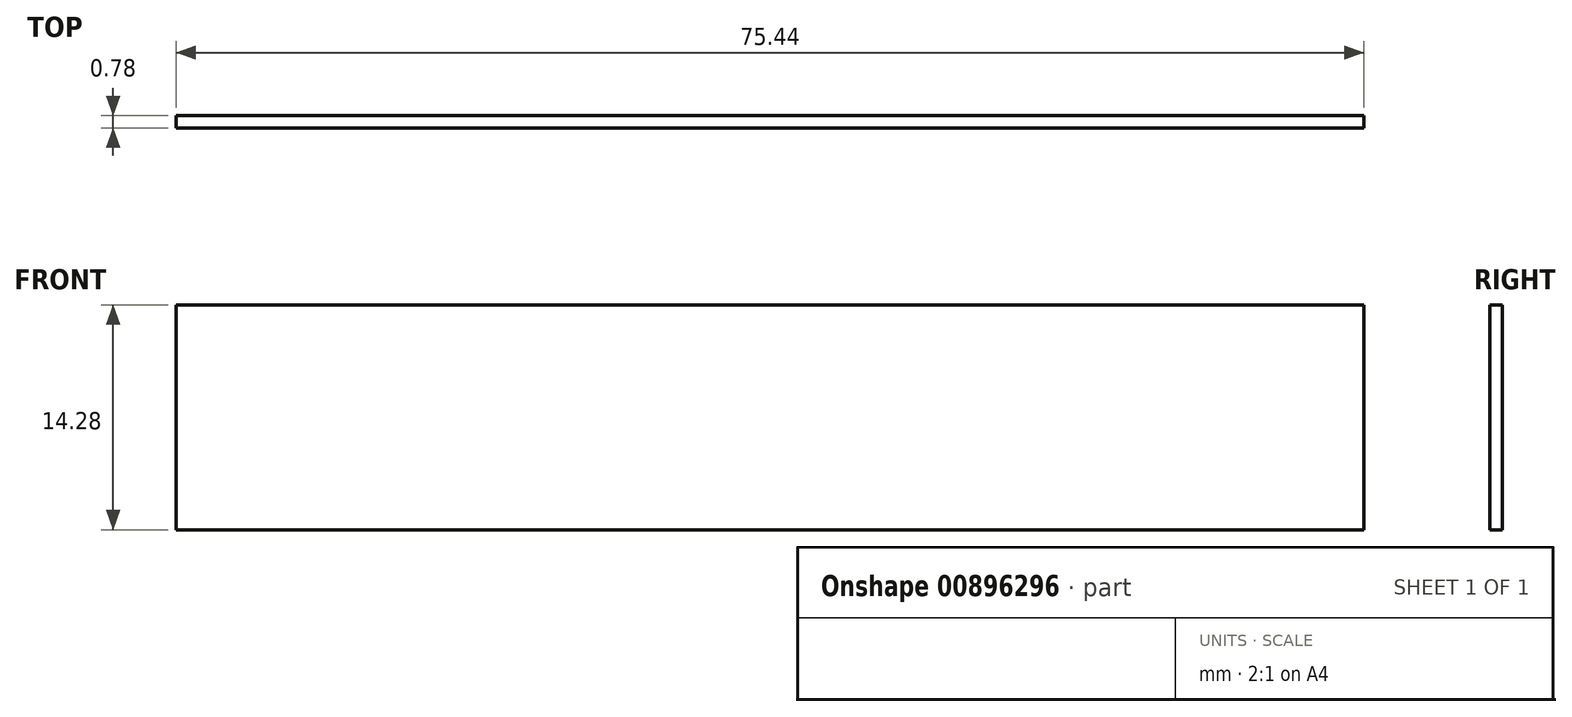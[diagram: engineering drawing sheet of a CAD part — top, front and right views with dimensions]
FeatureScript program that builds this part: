
annotation { "Feature Type Name" : "Feature", "Feature Type Description" : "" }
export const myFeature = defineFeature(function(context is Context, id is Id, definition is map)
    precondition{}
    {
        {
            var Q0;
            Q0=qCreatedBy(makeId("Front.planeOp"),FACE);
            var sketch = newSketch(context, id + "F0", { "sketchPlane" : qUnion([Q0])});
            skLineSegment(sketch, "E0.bottom", {"start": v(37.72, -7.14) * mm, "end": v(-37.72, -7.14) * mm});
            skLineSegment(sketch, "E0.top", {"start": v(37.72, 7.14) * mm, "end": v(-37.72, 7.14) * mm});
            skLineSegment(sketch, "E0.left", {"start": v(37.72, -7.14) * mm, "end": v(37.72, 7.14) * mm});
            skLineSegment(sketch, "E0.right", {"start": v(-37.72, -7.14) * mm, "end": v(-37.72, 7.14) * mm});
            skPoint(sketch, "E0.middle", {"position": v(0, 0) * mm});
            skSolve(sketch);
        }
        {
            var Q0;
            Q0 = qSketchRegion(id + "F0", true);
            extrude(context, id + "F1", {"entities" : qUnion([Q0]), "endBound" : BoundingType.SYMMETRIC, "depth" : 0.79 * mm, "offsetDistance" : 25.4 * mm});
        }
    });
